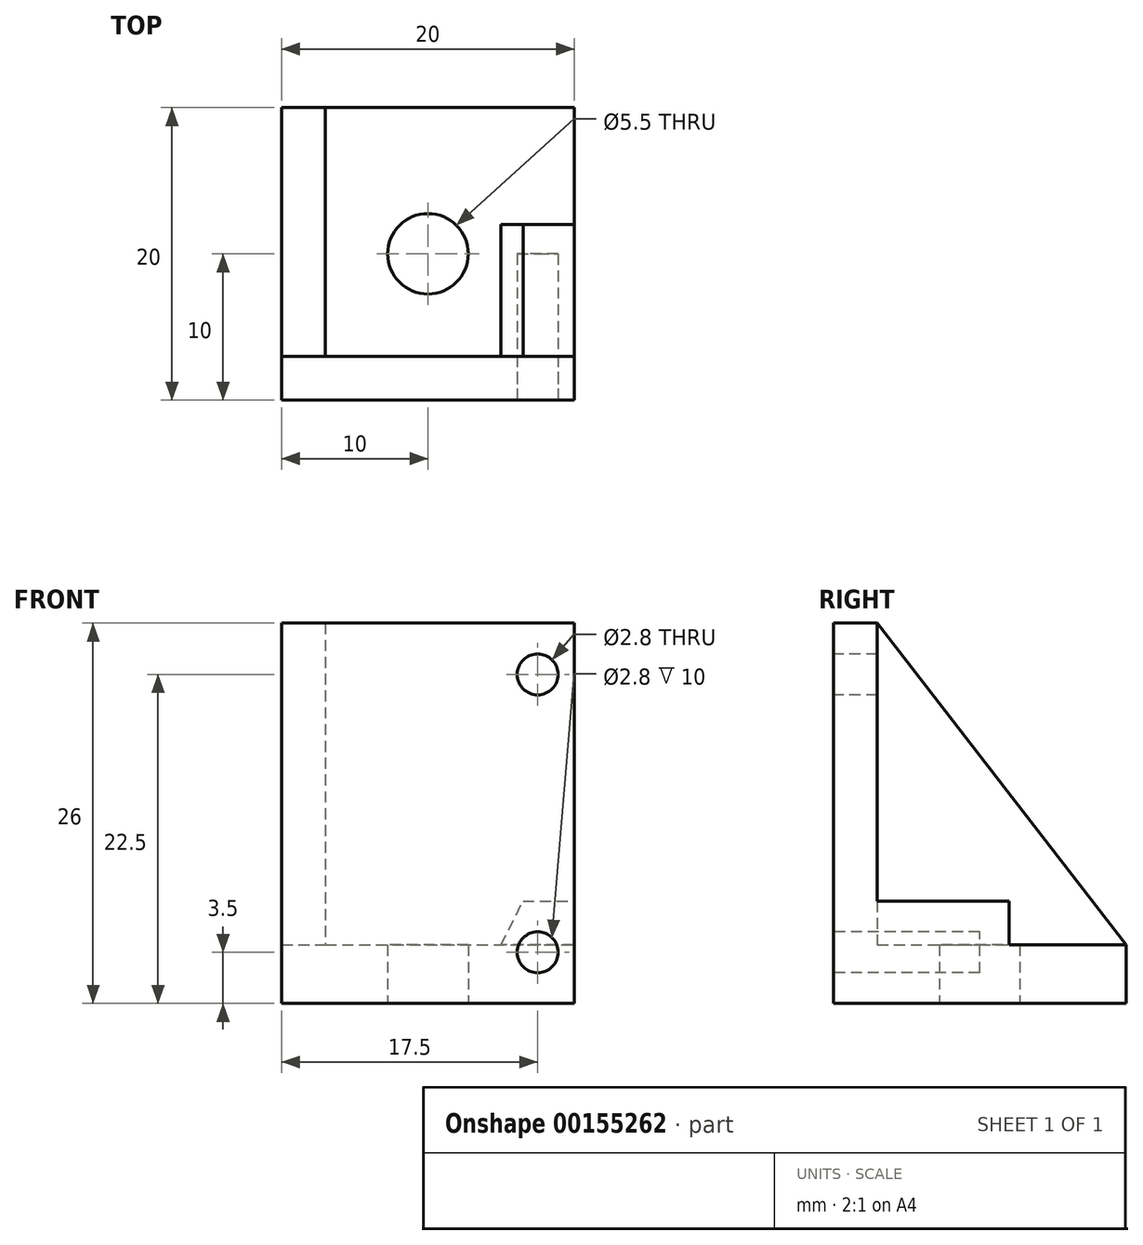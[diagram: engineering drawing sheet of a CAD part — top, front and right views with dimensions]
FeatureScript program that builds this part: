
annotation { "Feature Type Name" : "Feature", "Feature Type Description" : "" }
export const myFeature = defineFeature(function(context is Context, id is Id, definition is map)
    precondition{}
    {
        {
            var Q0;
            Q0=qCreatedBy(makeId("Top.planeOp"),FACE);
            var sketch = newSketch(context, id + "F0", { "sketchPlane" : qUnion([Q0])});
            skLineSegment(sketch, "E0.bottom", {"start": v(0, 0) * mm, "end": v(20, 0) * mm});
            skLineSegment(sketch, "E0.top", {"start": v(0, 20) * mm, "end": v(20, 20) * mm});
            skLineSegment(sketch, "E0.left", {"start": v(0, 0) * mm, "end": v(0, 20) * mm});
            skLineSegment(sketch, "E0.right", {"start": v(20, 0) * mm, "end": v(20, 20) * mm});
            skLineSegment(sketch, "E1", {"start": v(0, 20) * mm, "end": v(20, 0) * mm, "construction": true});
            skLineSegment(sketch, "E2", {"start": v(0, 0) * mm, "end": v(20, 20) * mm, "construction": true});
            skCircle(sketch, "E3", {"center": v(10, 10) * mm, "radius": 2.75 * mm});
            skSolve(sketch);
        }
        {
            var Q0;
            Q0 = qSketchRegion(id + "F0", true);
            extrude(context, id + "F1", {"entities" : qUnion([Q0]), "depth" : 4 * mm});
        }
        {
            var Q0;
            Q0=makeQuery(id+"F1.opExtrude","SWEPT_FACE",FACE,{"disambiguationData":[OSD([sQuery(id+"F0.wireOp",EDGE,"E0.bottom")])]});
            var sketch = newSketch(context, id + "F2", { "sketchPlane" : qUnion([Q0])});
            skLineSegment(sketch, "E4.bottom", {"start": v(0, 0) * mm, "end": v(20, 0) * mm});
            skLineSegment(sketch, "E4.top", {"start": v(0, 26) * mm, "end": v(20, 26) * mm});
            skLineSegment(sketch, "E4.left", {"start": v(0, 0) * mm, "end": v(0, 26) * mm});
            skLineSegment(sketch, "E4.right", {"start": v(20, 0) * mm, "end": v(20, 26) * mm});
            skSolve(sketch);
        }
        {
            var Q0;
            Q0 = qSketchRegion(id + "F2", true);
            extrude(context, id + "F3", {"entities" : qUnion([Q0]), "operationType" : NewBodyOperationType.ADD, "oppositeDirection" : true, "depth" : 3 * mm});
        }
        {
            var Q0;
            Q0=makeQuery(id+"F3.boolean.opBoolean","MERGE",FACE,{"derivedFrom":[makeQuery(id+"F1.opExtrude","SWEPT_FACE",FACE,{"disambiguationData":[OSD([sQuery(id+"F0.wireOp",EDGE,"E0.bottom")])]}),makeQuery(id+"F3.opExtrude","CAP_FACE",FACE,{"disambiguationData":[OSD([sQuery(id+"F2.wireOp",EDGE,"E4.bottom"),sQuery(id+"F2.wireOp",EDGE,"E4.top"),sQuery(id+"F2.wireOp",EDGE,"E4.left"),sQuery(id+"F2.wireOp",EDGE,"E4.right")])],"isStart":true})]});
            var sketch = newSketch(context, id + "F4", { "sketchPlane" : qUnion([Q0])});
            skLineSegment(sketch, "E5", {"start": v(17.5, 26) * mm, "end": v(17.5, 0) * mm, "construction": true});
            skCircle(sketch, "E6", {"center": v(17.5, 3.5) * mm, "radius": 1.4 * mm});
            skCircle(sketch, "E7", {"center": v(17.5, 22.5) * mm, "radius": 1.4 * mm});
            skSolve(sketch);
        }
        {
            var Q0;
            Q0=makeQuery(id+"F1.opExtrude","CAP_FACE",FACE,{"disambiguationData":[OSD([sQuery(id+"F0.wireOp",EDGE,"E0.bottom"),sQuery(id+"F0.wireOp",EDGE,"E0.top"),sQuery(id+"F0.wireOp",EDGE,"E0.left"),sQuery(id+"F0.wireOp",EDGE,"E0.right"),sQuery(id+"F0.wireOp",EDGE,"E3")])],"isStart":false});
            var sketch = newSketch(context, id + "F5", { "sketchPlane" : qUnion([Q0])});
            skLineSegment(sketch, "E8.bottom", {"start": v(20, 3) * mm, "end": v(15, 3) * mm});
            skLineSegment(sketch, "E8.top", {"start": v(20, 12) * mm, "end": v(15, 12) * mm});
            skLineSegment(sketch, "E8.left", {"start": v(20, 3) * mm, "end": v(20, 12) * mm});
            skLineSegment(sketch, "E8.right", {"start": v(15, 3) * mm, "end": v(15, 12) * mm});
            skSolve(sketch);
        }
        {
            var Q0;
            Q0 = qSketchRegion(id + "F5", true);
            extrude(context, id + "F6", {"entities" : qUnion([Q0]), "operationType" : NewBodyOperationType.ADD, "depth" : 3 * mm});
        }
        {
            var Q0;
            Q0 = qSketchRegion(id + "F4", true);
            extrude(context, id + "F7", {"entities" : qUnion([Q0]), "operationType" : NewBodyOperationType.REMOVE, "oppositeDirection" : true, "depth" : 10 * mm});
        }
        {
            var Q0;
            Q0=makeQuery(id+"F3.boolean.opBoolean","MERGE",FACE,{"derivedFrom":[makeQuery(id+"F1.opExtrude","SWEPT_FACE",FACE,{"disambiguationData":[OSD([sQuery(id+"F0.wireOp",EDGE,"E0.left")])]}),makeQuery(id+"F3.opExtrude","SWEPT_FACE",FACE,{"disambiguationData":[OSD([sQuery(id+"F2.wireOp",EDGE,"E4.left")])]})]});
            var sketch = newSketch(context, id + "F8", { "sketchPlane" : qUnion([Q0])});
            skLineSegment(sketch, "E9", {"start": v(-3, 26) * mm, "end": v(-20, 4) * mm});
            skLineSegment(sketch, "E10", {"start": v(-20, 4) * mm, "end": v(-3, 4) * mm});
            skLineSegment(sketch, "E11", {"start": v(-3, 4) * mm, "end": v(-3, 26) * mm});
            skSolve(sketch);
        }
        {
            var Q0;
            Q0 = qSketchRegion(id + "F8", true);
            extrude(context, id + "F9", {"entities" : qUnion([Q0]), "operationType" : NewBodyOperationType.ADD, "oppositeDirection" : true, "depth" : 3 * mm});
        }
        {
            var Q0;
            Q0=makeQuery(id+"F6.opExtrude","CAP_EDGE",EDGE,{"disambiguationData":[OSD([sQuery(id+"F5.wireOp",EDGE,"E8.right")])],"isStart":false});
            chamfer(context, id + "F10", {"entities" : qUnion([Q0]), "chamferType" : ChamferType.TWO_OFFSETS, "width1" : 3 * mm, "oppositeDirection" : false, "width2" : 1.5 * mm, "tangentPropagation" : true});
        }
    });
